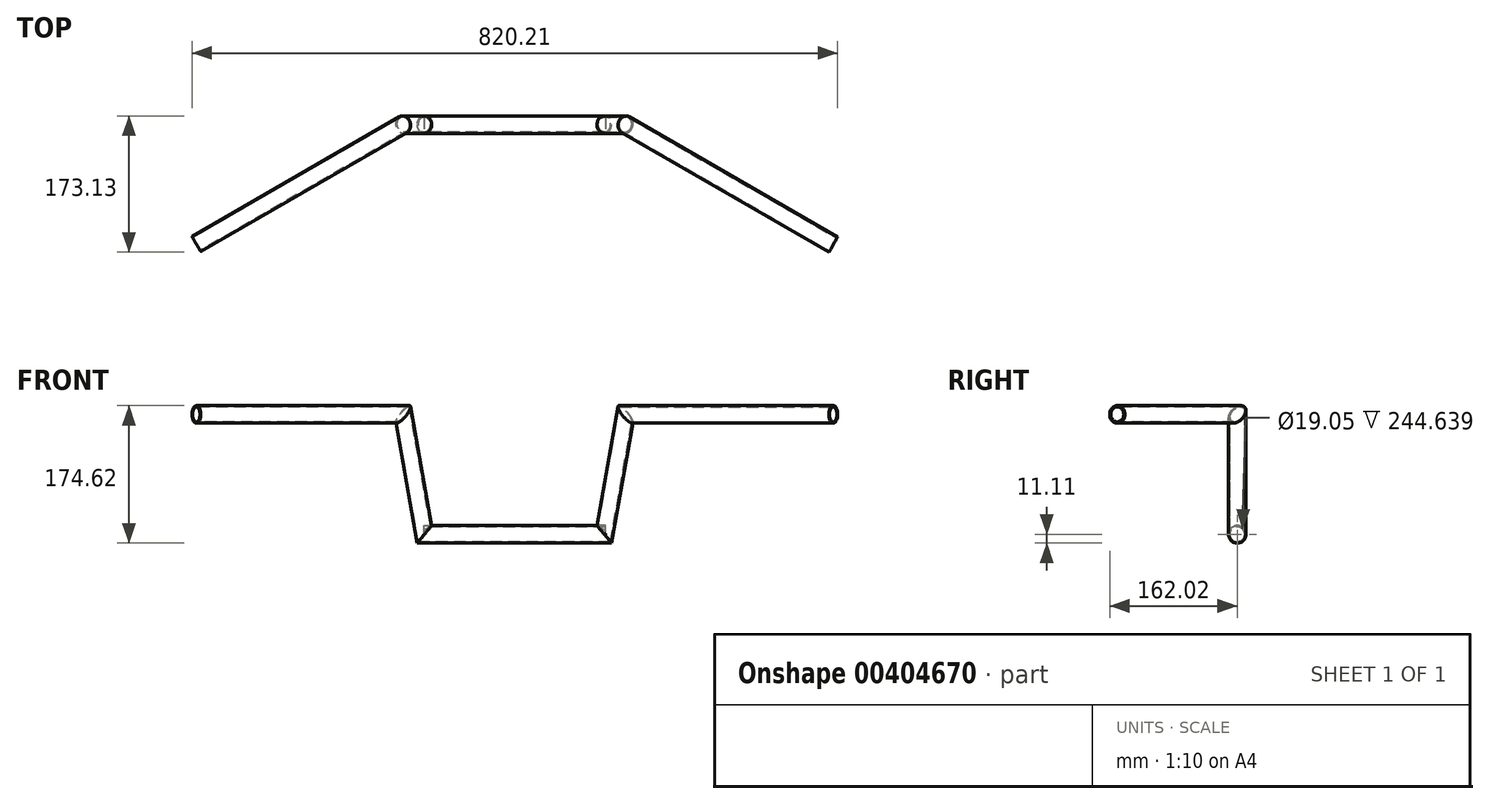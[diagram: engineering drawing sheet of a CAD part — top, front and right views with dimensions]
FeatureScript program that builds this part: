
annotation { "Feature Type Name" : "Feature", "Feature Type Description" : "" }
export const myFeature = defineFeature(function(context is Context, id is Id, definition is map)
    precondition{}
    {
        {
            var Q0;
            Q0=qCreatedBy(makeId("Front.planeOp"),FACE);
            var sketch = newSketch(context, id + "F0", { "sketchPlane" : qUnion([Q0])});
            skLineSegment(sketch, "E0", {"start": v(-115.67, 0) * mm, "end": v(112.93, 0) * mm});
            skLineSegment(sketch, "E1", {"start": v(112.93, 0) * mm, "end": v(139.8, 152.4) * mm});
            skLineSegment(sketch, "E2", {"start": v(-115.67, 0) * mm, "end": v(-142.54, 152.4) * mm});
            skSolve(sketch);
        }
        {
            var Q0;
            Q0=qCreatedBy(makeId("Right.planeOp"),FACE);
            cPlane(context, id + "F1", {"entities" : qUnion([Q0]), "cplaneType" : CPlaneType.OFFSET, "offset" : 114.3 * mm, "width" : 152.4 * mm, "height" : 152.4 * mm});
        }
        {
            var Q0;
            Q0=qCreatedBy(id+"F1.planeOp",FACE);
            var sketch = newSketch(context, id + "F2", { "sketchPlane" : qUnion([Q0])});
            skCircle(sketch, "E3", {"center": v(0, 0) * mm, "radius": 11.11 * mm});
            skCircle(sketch, "E4", {"center": v(0, 0) * mm, "radius": 9.53 * mm});
            skSolve(sketch);
        }
        {
            var Q0;
            Q0=qCreatedBy(makeId("Top.planeOp"),FACE);
            cPlane(context, id + "F3", {"entities" : qUnion([Q0]), "cplaneType" : CPlaneType.OFFSET, "offset" : 152.4 * mm, "width" : 152.4 * mm, "height" : 152.4 * mm});
        }
        {
            var Q0;
            Q0=qCreatedBy(id+"F3.planeOp",FACE);
            var sketch = newSketch(context, id + "F4", { "sketchPlane" : qUnion([Q0])});
            skLineSegment(sketch, "E5", {"start": v(-142.54, 0) * mm, "end": v(-406.5, -152.4) * mm});
            skLineSegment(sketch, "E6", {"start": v(139.8, 0) * mm, "end": v(403.77, -152.4) * mm});
            skLineSegment(sketch, "E7", {"start": v(139.8, 0) * mm, "end": v(-214.17, 0) * mm, "construction": true});
            skSolve(sketch);
        }
        {
            var Q0;
            Q0=makeQuery(id+"F2.imprint","IMPRINT",FACE,{"disambiguationData":[TD([[makeQuery(id+"F2.imprint","IMPRINT",EDGE,{"derivedFrom":sQuery(id+"F2.wireOp",EDGE,"E3")}),1.0]])]});
            var Q1;
            Q1=sQuery(id+"F0.wireOp",EDGE,"E0");
            var Q2;
            Q2=sQuery(id+"F0.wireOp",EDGE,"E2");
            var Q3;
            Q3=sQuery(id+"F4.wireOp",EDGE,"E5");
            sweep(context, id + "F5", {"profiles" : qUnion([Q0]), "path" : qUnion([Q1, Q2, Q3])});
        }
        {
            var Q0;
            Q0=qCreatedBy(makeId("Right.planeOp"),FACE);
            cPlane(context, id + "F6", {"entities" : qUnion([Q0]), "cplaneType" : CPlaneType.OFFSET, "offset" : 114.3 * mm, "oppositeDirection" : true, "width" : 152.4 * mm, "height" : 152.4 * mm});
        }
        {
            var Q0;
            Q0=qCreatedBy(id+"F6.planeOp",FACE);
            var sketch = newSketch(context, id + "F7", { "sketchPlane" : qUnion([Q0])});
            skCircle(sketch, "E8", {"center": v(0, 0) * mm, "radius": 11.11 * mm});
            skCircle(sketch, "E9", {"center": v(0, 0) * mm, "radius": 9.53 * mm});
            skSolve(sketch);
        }
        {
            var Q0;
            Q0 = qSketchRegion(id + "F7", true);
            var Q1;
            Q1=sQuery(id+"F0.wireOp",EDGE,"E0");
            var Q2;
            Q2=sQuery(id+"F0.wireOp",EDGE,"E1");
            var Q3;
            Q3=sQuery(id+"F4.wireOp",EDGE,"E6");
            sweep(context, id + "F8", {"operationType" : NewBodyOperationType.ADD, "profiles" : qUnion([Q0]), "path" : qUnion([Q1, Q2, Q3])});
        }
    });
